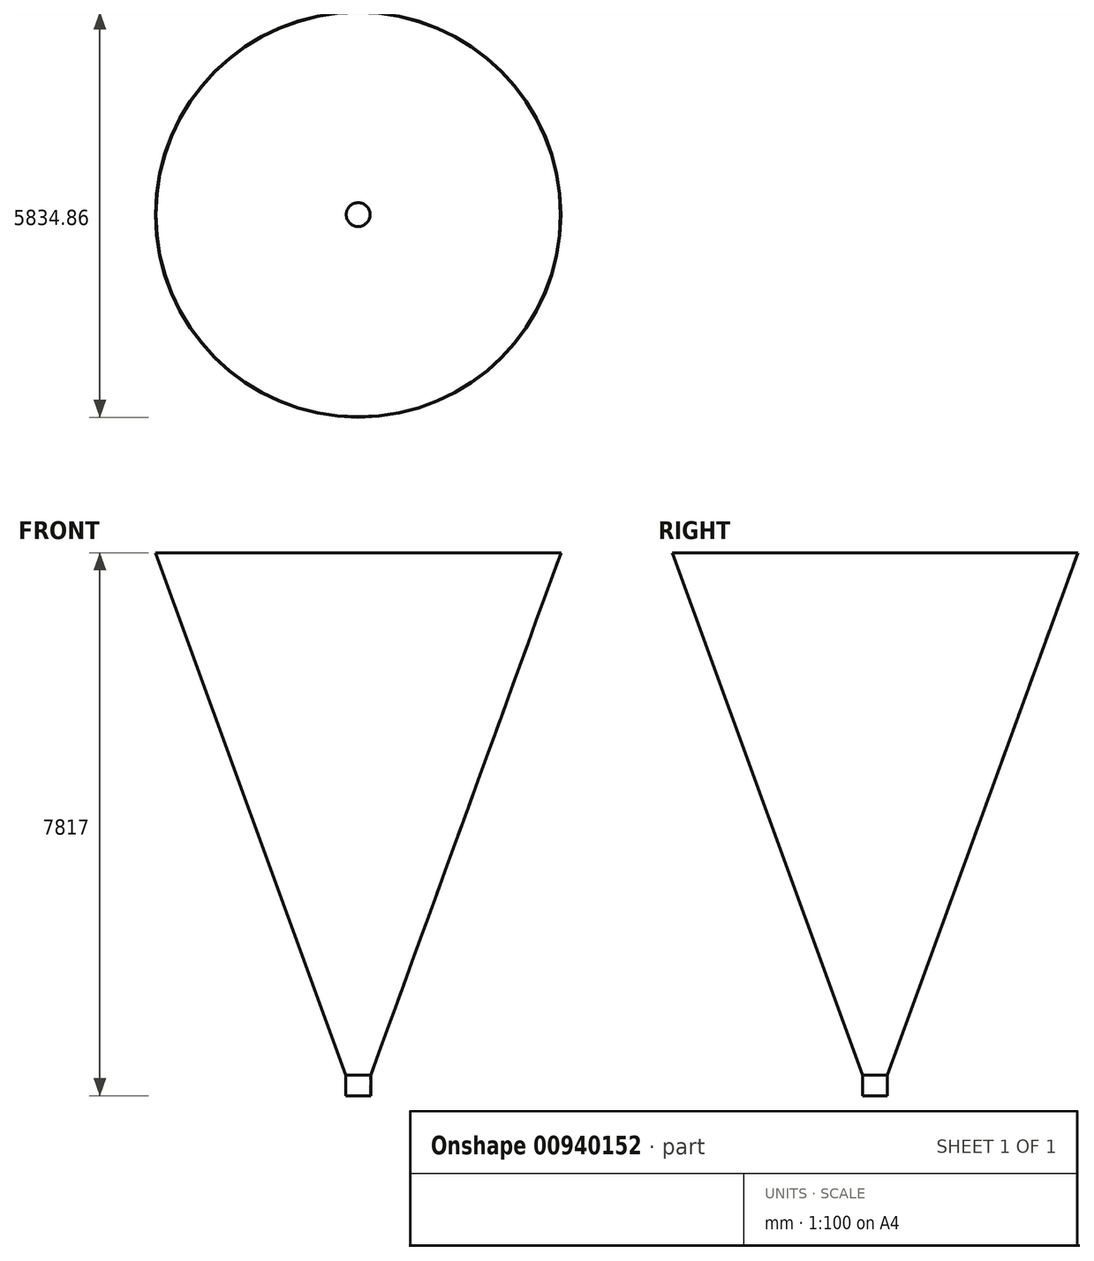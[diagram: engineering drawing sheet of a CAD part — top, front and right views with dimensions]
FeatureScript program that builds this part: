
annotation { "Feature Type Name" : "Feature", "Feature Type Description" : "" }
export const myFeature = defineFeature(function(context is Context, id is Id, definition is map)
    precondition{}
    {
        {
            var Q0;
            Q0=qCreatedBy(makeId("Front.planeOp"),FACE);
            var sketch = newSketch(context, id + "F0", { "sketchPlane" : qUnion([Q0])});
            skLineSegment(sketch, "E0", {"start": v(0, 0) * mm, "end": v(-171.5, 0) * mm, "construction": true});
            skLineSegment(sketch, "E1", {"start": v(-171.5, 0) * mm, "end": v(-171.5, 296) * mm});
            skLineSegment(sketch, "E2", {"start": v(-171.5, 296) * mm, "end": v(-2908.92, 7817) * mm});
            skLineSegment(sketch, "E3", {"start": v(-2908.92, 7817) * mm, "end": v(0, 7817) * mm});
            skLineSegment(sketch, "E4", {"start": v(0, 7817) * mm, "end": v(0, 0) * mm, "construction": true});
            skLineSegment(sketch, "E5", {"start": v(-171.5, 0) * mm, "end": v(-179.5, 0) * mm});
            skLineSegment(sketch, "E6", {"start": v(-179.5, 0) * mm, "end": v(-179.5, 294.59) * mm});
            skLineSegment(sketch, "E7", {"start": v(-179.5, 294.59) * mm, "end": v(-2917.43, 7817) * mm});
            skPoint(sketch, "E7.endSnap0", {"position": v(-1454.46, 7817) * mm});
            skLineSegment(sketch, "E8", {"start": v(-2917.43, 7817) * mm, "end": v(-2908.92, 7817) * mm});
            skSolve(sketch);
        }
        {
            var Q0;
            Q0=qSketchRegion(id+"F0",true);
            var Q1;
            Q1=sQuery(id+"F0.wireOp",EDGE,"E4");
            revolve(context, id + "F1", {"entities" : qUnion([Q0]), "axis" : qUnion([Q1]), "revolveType" : RevolveType.FULL});
        }
    });
